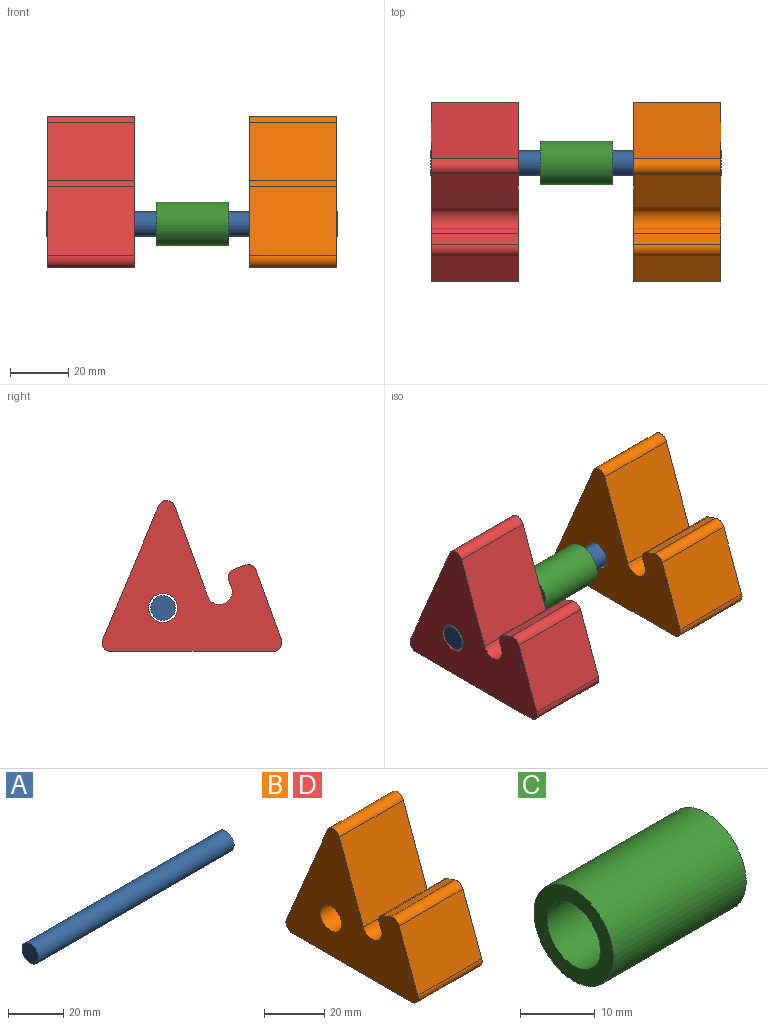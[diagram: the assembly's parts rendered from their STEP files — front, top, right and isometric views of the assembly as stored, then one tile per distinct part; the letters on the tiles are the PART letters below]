
ASSEMBLY  parts=4 mates=3
PART A: 3 faces, bbox 100x8.5x8.5 mm
  f0: cylinder r=4.25mm len=100mm, axis (-1,0,0), area 2670.4mm2, adj f1,f2
  f1: plane 8.5x8.5mm, normal (1,0,0), area 56.7mm2, adj f0
  f2: plane 8.5x8.5mm, normal (-1,0,0), area 56.7mm2, adj f0
PART B: 15 faces, bbox 30x62x52.1 mm
  f0: plane 46.05x30mm, normal (0,0.92,0.39), area 1498mm2, adj f6,f7,f8,f12
  f1: plane 30.97x30mm, normal (0,-0.94,0.34), area 988.7mm2, adj f6,f7,f8,f14
  f2: plane 30x2.47mm, normal (0,0.94,-0.34), area 78.8mm2, adj f6,f7,f9,f14
  f3: plane 30x3.76mm, normal (0,0.34,0.94), area 120mm2, adj f6,f7,f9,f10
  f4: plane 30x23.96mm, normal (0,-0.94,0.34), area 765.1mm2, adj f6,f7,f10,f11
  f5: plane 56.01x30mm, normal (0,0,-1), area 1680.4mm2, adj f6,f7,f11,f12
  f6: plane 62.01x52.05mm, normal (1,0,0), area 1652.8mm2, adj f0,f1,f2,f3,f4,f5,f8,f9
  f7: plane 62.01x52.05mm, normal (-1,0,0), area 1652.8mm2, adj f0,f1,f2,f3,f4,f5,f8,f9
  f8: cylinder r=3mm len=30mm, axis (-1,0,0), area 215.6mm2, adj f0,f1,f6,f7
  f9: cylinder r=3mm len=30mm, axis (-1,0,0), area 141.4mm2, adj f2,f3,f6,f7
  f10: cylinder r=3mm len=30mm, axis (-1,0,0), area 141.4mm2, adj f3,f4,f6,f7
  f11: cylinder r=3mm len=30mm, axis (-1,0,0), area 172.8mm2, adj f4,f5,f6,f7
  f12: cylinder r=3mm len=30mm, axis (-1,0,0), area 177.1mm2, adj f0,f5,f6,f7
  f13: cylinder r=5mm len=30mm, axis (1,0,0), area 942.5mm2, adj f6,f7
  f14: cylinder r=4.38mm len=30mm, axis (1,0,0), area 412.3mm2, adj f1,f2,f6,f7
PART C: 4 faces, bbox 25x15x15 mm
  f0: cylinder r=7.5mm len=25mm, axis (-1,0,0), area 1178.1mm2, adj f1,f2
  f1: plane 15x15mm, normal (1,0,0), area 98.2mm2, adj f0,f3
  f2: plane 15x15mm, normal (-1,0,0), area 98.2mm2, adj f0,f3
  f3: cylinder r=5mm len=25mm, axis (-1,0,0), area 785.4mm2, adj f1,f2
PART D: same geometry as B
PLACE A rot(axis=(0.95,-0.02,0.3),0deg) t=(-74.57,24.25,17.23)mm
PLACE B t=(-4.69,52.8,2.23)mm
PLACE C rot(axis=(0.95,-0.02,0.3),0deg) t=(-36.82,24.25,17.23)mm
PLACE D t=(-74.54,52.8,2.23)mm
MATE cylindrical B.f13 <-> A.f0  axis (1,0,0) through (25.31,24.25,17.23)mm
MATE cylindrical D.f13 <-> A.f0  axis (-1,0,0) through (-74.54,24.25,17.23)mm
MATE slider C.f0 <-> A.f0  axis (-1,0,0) through (-24.32,24.25,17.23)mm
